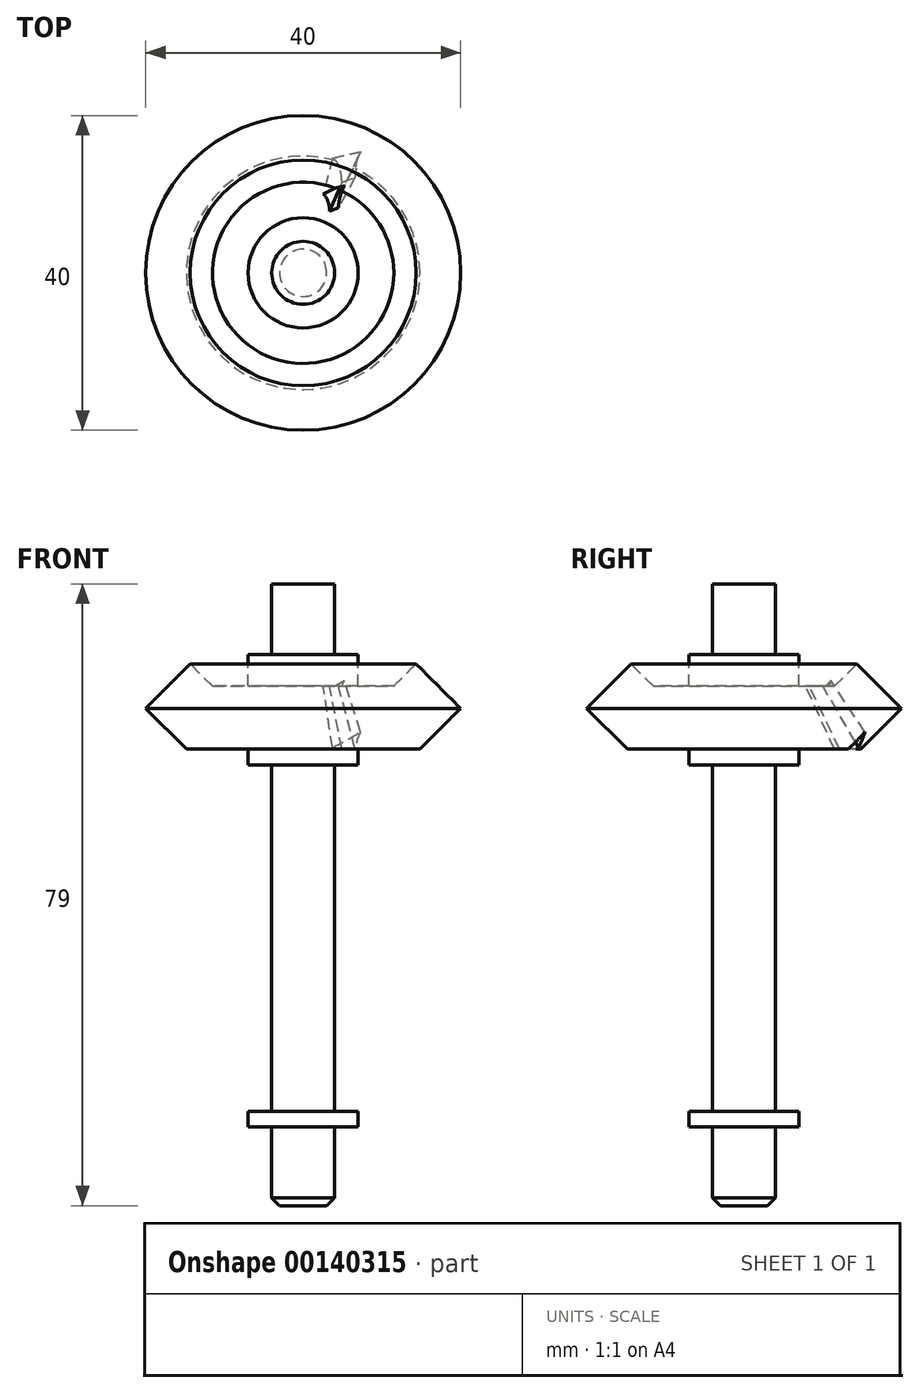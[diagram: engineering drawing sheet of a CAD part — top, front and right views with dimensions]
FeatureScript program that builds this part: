
annotation { "Feature Type Name" : "Feature", "Feature Type Description" : "" }
export const myFeature = defineFeature(function(context is Context, id is Id, definition is map)
    precondition{}
    {
        {
            var Q0;
            Q0=qCreatedBy(makeId("Front.planeOp"),FACE);
            var sketch = newSketch(context, id + "F0", { "sketchPlane" : qUnion([Q0])});
            skLineSegment(sketch, "E0", {"start": v(0, 50) * mm, "end": v(0, -50) * mm, "construction": true});
            skSolve(sketch);
        }
        {
            var Q0;
            Q0=qCreatedBy(makeId("Front.planeOp"),FACE);
            var sketch = newSketch(context, id + "F1", { "sketchPlane" : qUnion([Q0])});
            skLineSegment(sketch, "E1", {"start": v(0, 0) * mm, "end": v(0, 8) * mm});
            skLineSegment(sketch, "E2", {"start": v(0, 8) * mm, "end": v(11.51, 8) * mm});
            skLineSegment(sketch, "E3", {"start": v(14.83, 0) * mm, "end": v(0, 0) * mm});
            skLineSegment(sketch, "E4", {"start": v(11.51, 8) * mm, "end": v(14.34, 10.83) * mm});
            skLineSegment(sketch, "E5", {"start": v(14.34, 10.83) * mm, "end": v(20, 5.17) * mm});
            skLineSegment(sketch, "E6", {"start": v(20, 5.17) * mm, "end": v(14.83, 0) * mm});
            skSolve(sketch);
        }
        {
            var Q0;
            Q0=makeQuery(id+"F1.imprint","IMPRINT",FACE,{"disambiguationData":[TD([[makeQuery(id+"F1.imprint","IMPRINT",EDGE,{"derivedFrom":sQuery(id+"F1.wireOp",EDGE,"E1")}),-1.0]])]});
            var Q1;
            Q1=sQuery(id+"F0.wireOp",EDGE,"E0");
            revolve(context, id + "F2", {"entities" : qUnion([Q0]), "axis" : qUnion([Q1]), "revolveType" : RevolveType.FULL});
        }
        {
            var Q0;
            Q0=sQuery(id+"F1.wireOp",EDGE,"E5");
            var Q1;
            Q1=sQuery(id+"F1.wireOp",VERTEX,"E6.start");
            cPlane(context, id + "F3", {"entities" : qUnion([Q0, Q1]), "cplaneType" : CPlaneType.LINE_POINT, "offset" : 25 * mm, "width" : 150 * mm, "height" : 150 * mm});
        }
        {
            var Q0;
            Q0=qCreatedBy(id+"F3.planeOp",FACE);
            var sketch = newSketch(context, id + "F4", { "sketchPlane" : qUnion([Q0])});
            skLineSegment(sketch, "E7", {"start": v(15.3, 1.25) * mm, "end": v(15.3, -1.25) * mm});
            skLineSegment(sketch, "E8", {"start": v(20.3, -3.16) * mm, "end": v(20.3, 3.16) * mm});
            skLineSegment(sketch, "E9", {"start": v(14.27, 0) * mm, "end": v(19.27, 0) * mm, "construction": true});
            skArc(sketch, "E10", {"start": v(20.3, -3.16) * mm, "mid": v(17.98, -1.74) * mm, "end": v(15.3, -1.25) * mm});
            skArc(sketch, "E11.MirrorCS", {"start": v(20.3, 3.16) * mm, "mid": v(17.98, 1.74) * mm, "end": v(15.3, 1.25) * mm});
            skSolve(sketch);
        }
        {
            var Q0;
            Q0=qCreatedBy(makeId("Front.planeOp"),FACE);
            var sketch = newSketch(context, id + "F5", { "sketchPlane" : qUnion([Q0])});
            skLineSegment(sketch, "E12", {"start": v(0, 25.17) * mm, "end": v(75.17, -50) * mm, "construction": true});
            skSolve(sketch);
        }
        {
            var Q1;
            Q1=makeQuery(id+"F4.imprint","IMPRINT",FACE,{"disambiguationData":[TD([[makeQuery(id+"F4.imprint","IMPRINT",EDGE,{"derivedFrom":sQuery(id+"F4.wireOp",EDGE,"E7")}),1.0]])]});
            var Q2;
            Q2=sQuery(id+"F5.wireOp",VERTEX,"E12.start");
            loft(context, id + "F6", {"operationType" : NewBodyOperationType.REMOVE, "sheetProfilesArray" : [{ "sheetProfileEntities" : qUnion([Q1]) }, { "sheetProfileEntities" : qUnion([Q2]) }]});
        }
        {
            var Q0;
            Q0=qCreatedBy(makeId("Front.planeOp"),FACE);
            var sketch = newSketch(context, id + "F7", { "sketchPlane" : qUnion([Q0])});
            skLineSegment(sketch, "E13.bottom", {"start": v(4, 12) * mm, "end": v(7, 12) * mm});
            skLineSegment(sketch, "E13.top", {"start": v(4, -2) * mm, "end": v(7, -2) * mm});
            skLineSegment(sketch, "E13.right", {"start": v(7, 12) * mm, "end": v(7, -2) * mm});
            skLineSegment(sketch, "E14.bottom", {"start": v(0, 21) * mm, "end": v(4, 21) * mm});
            skLineSegment(sketch, "E14.top", {"start": v(0, -58) * mm, "end": v(4, -58) * mm});
            skLineSegment(sketch, "E14.left", {"start": v(0, 21) * mm, "end": v(0, -58) * mm});
            skLineSegment(sketch, "E14.right", {"start": v(4, 21) * mm, "end": v(4, 12) * mm});
            skLineSegment(sketch, "E15.trimOffspring", {"start": v(4, -2) * mm, "end": v(4, -46) * mm});
            skLineSegment(sketch, "E16.bottom", {"start": v(4, -46) * mm, "end": v(7, -46) * mm});
            skLineSegment(sketch, "E16.top", {"start": v(4, -48) * mm, "end": v(7, -48) * mm});
            skLineSegment(sketch, "E16.right", {"start": v(7, -46) * mm, "end": v(7, -48) * mm});
            skLineSegment(sketch, "E17.trimOffspring", {"start": v(4, -48) * mm, "end": v(4, -58) * mm});
            skSolve(sketch);
        }
        {
            var Q0;
            Q0=makeQuery(id+"F7.imprint","IMPRINT",FACE,{"disambiguationData":[TD([[makeQuery(id+"F7.imprint","IMPRINT",EDGE,{"derivedFrom":sQuery(id+"F7.wireOp",EDGE,"E13.bottom")}),-1.0]])]});
            var Q1;
            Q1=sQuery(id+"F0.wireOp",EDGE,"E0");
            revolve(context, id + "F8", {"operationType" : NewBodyOperationType.ADD, "entities" : qUnion([Q0]), "axis" : qUnion([Q1]), "revolveType" : RevolveType.FULL});
        }
        {
            var Q0;
            Q0=makeQuery(id+"F8.opRevolve","SWEPT_EDGE",EDGE,{"disambiguationData":[OSD([sQuery(id+"F7.wireOp",EDGE,"E14.top"),sQuery(id+"F7.wireOp",EDGE,"E17.trimOffspring")])]});
            chamfer(context, id + "F9", {"entities" : qUnion([Q0]), "width" : 1 * mm, "tangentPropagation" : true});
        }
    });
